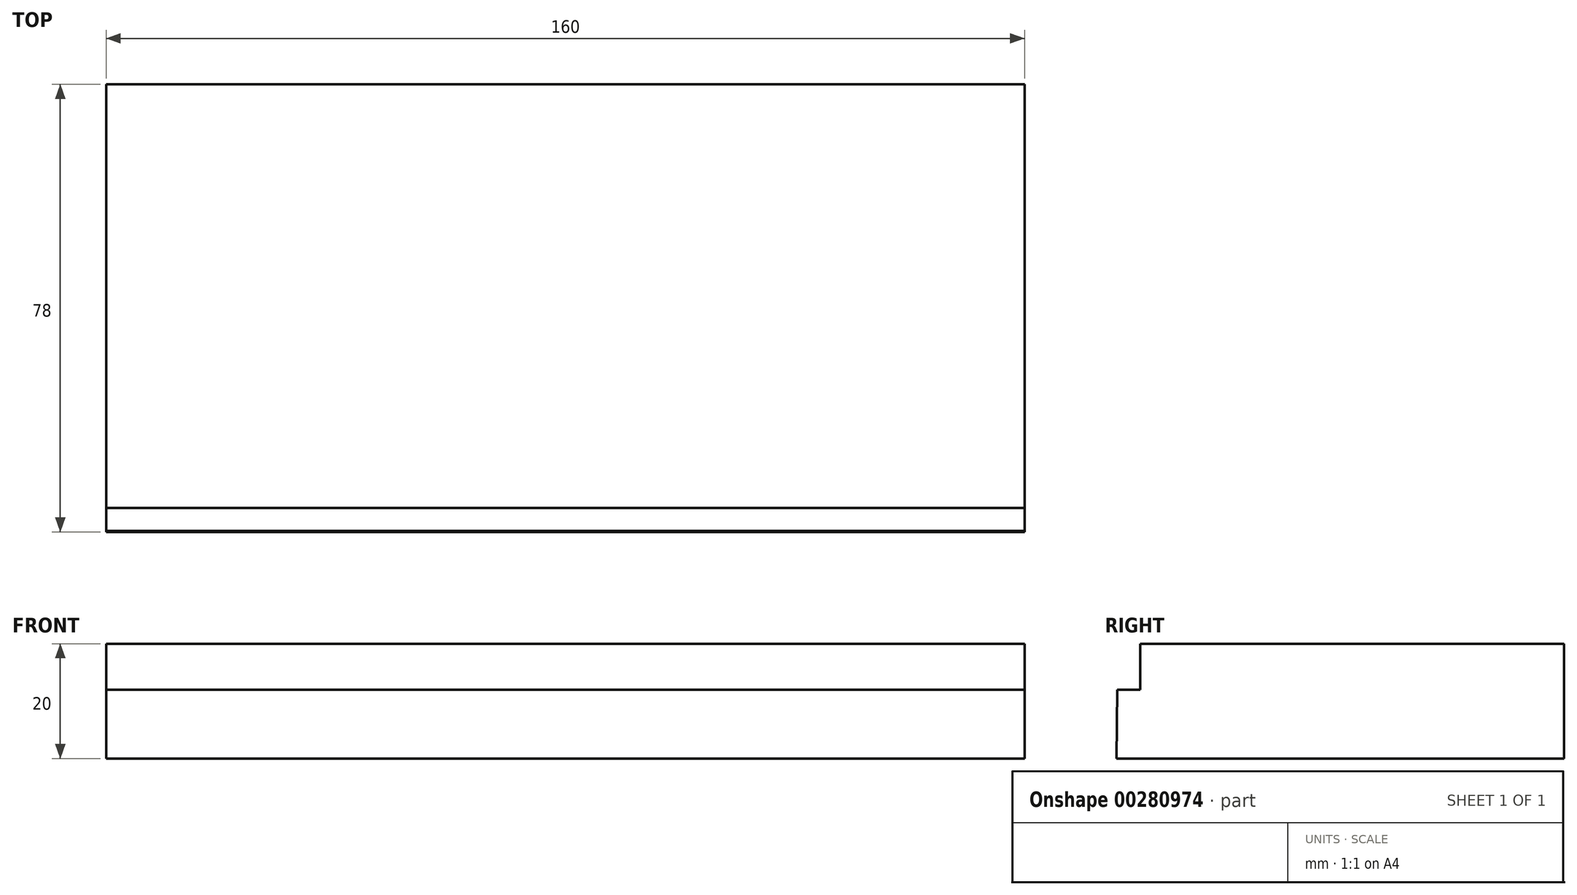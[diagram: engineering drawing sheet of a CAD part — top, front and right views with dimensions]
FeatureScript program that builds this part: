
annotation { "Feature Type Name" : "Feature", "Feature Type Description" : "" }
export const myFeature = defineFeature(function(context is Context, id is Id, definition is map)
    precondition{}
    {
        {
            var Q0;
            Q0=qCreatedBy(makeId("Right.planeOp"),FACE);
            var sketch = newSketch(context, id + "F0", { "sketchPlane" : qUnion([Q0])});
            skLineSegment(sketch, "E0", {"start": v(-23.8, 0) * mm, "end": v(-19.8, 0) * mm});
            skLineSegment(sketch, "E1", {"start": v(-19.8, 0) * mm, "end": v(-19.8, 8) * mm});
            skLineSegment(sketch, "E2", {"start": v(-19.8, 8) * mm, "end": v(54.07, 8) * mm});
            skLineSegment(sketch, "E3", {"start": v(54.07, 8) * mm, "end": v(54.07, -12) * mm});
            skLineSegment(sketch, "E4", {"start": v(54.07, -12) * mm, "end": v(-23.93, -12) * mm});
            skLineSegment(sketch, "E5", {"start": v(-23.93, -12) * mm, "end": v(-23.8, 0) * mm});
            skSolve(sketch);
        }
        {
            var Q0;
            Q0 = qSketchRegion(id + "F0", true);
            extrude(context, id + "F1", {"entities" : qUnion([Q0]), "depth" : 160 * mm});
        }
    });
